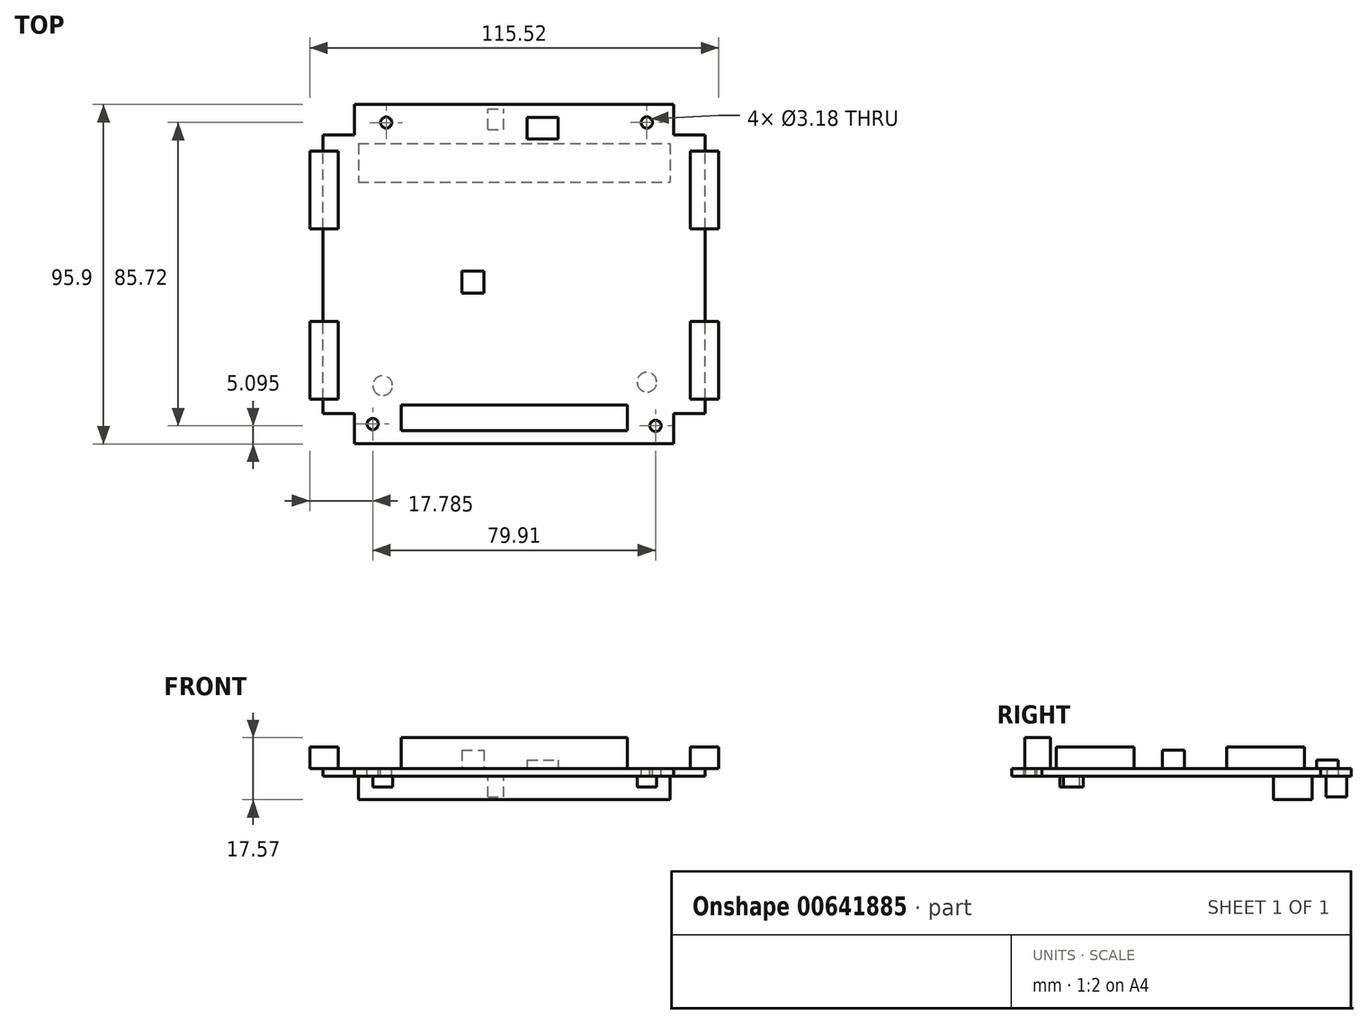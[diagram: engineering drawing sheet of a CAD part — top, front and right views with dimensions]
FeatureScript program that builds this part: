
annotation { "Feature Type Name" : "Feature", "Feature Type Description" : "" }
export const myFeature = defineFeature(function(context is Context, id is Id, definition is map)
    precondition{}
    {
        {
            var Q0;
            Q0=qCreatedBy(makeId("Top.planeOp"),FACE);
            var sketch = newSketch(context, id + "F0", { "sketchPlane" : qUnion([Q0])});
            skLineSegment(sketch, "E0.bottom", {"start": v(53.98, -39.42) * mm, "end": v(-53.97, -39.42) * mm});
            skLineSegment(sketch, "E0.top", {"start": v(53.97, 39.42) * mm, "end": v(-53.98, 39.42) * mm});
            skLineSegment(sketch, "E0.left", {"start": v(53.98, -39.42) * mm, "end": v(53.97, 39.42) * mm});
            skLineSegment(sketch, "E0.right", {"start": v(-53.97, -39.42) * mm, "end": v(-53.98, 39.42) * mm});
            skPoint(sketch, "E0.middle", {"position": v(0, 0) * mm});
            skLineSegment(sketch, "E1.bottom", {"start": v(45.09, -47.95) * mm, "end": v(-45.09, -47.95) * mm});
            skLineSegment(sketch, "E1.top", {"start": v(45.09, 47.95) * mm, "end": v(-45.09, 47.94) * mm});
            skLineSegment(sketch, "E1.left", {"start": v(45.09, -47.95) * mm, "end": v(45.09, 47.95) * mm});
            skLineSegment(sketch, "E1.right", {"start": v(-45.09, -47.95) * mm, "end": v(-45.09, 47.94) * mm});
            skSolve(sketch);
        }
        {
            var Q0;
            Q0 = qSketchRegion(id + "F0", true);
            extrude(context, id + "F1", {"entities" : qUnion([Q0]), "depth" : 2.24 * mm, "offsetDistance" : 25 * mm});
        }
        {
            var Q0;
            Q0=makeQuery(id+"F1.opExtrude","CAP_FACE",FACE,{"disambiguationData":[OSD([sQuery(id+"F0.wireOp",EDGE,"E0.bottom"),sQuery(id+"F0.wireOp",EDGE,"E0.top"),sQuery(id+"F0.wireOp",EDGE,"E0.left"),sQuery(id+"F0.wireOp",EDGE,"E0.right"),sQuery(id+"F0.wireOp",EDGE,"E1.bottom"),sQuery(id+"F0.wireOp",EDGE,"E1.top"),sQuery(id+"F0.wireOp",EDGE,"E1.left"),sQuery(id+"F0.wireOp",EDGE,"E1.right")])],"isStart":false});
            var sketch = newSketch(context, id + "F2", { "sketchPlane" : qUnion([Q0])});
            skLineSegment(sketch, "E2.bottom", {"start": v(49.72, -35.28) * mm, "end": v(57.76, -35.28) * mm});
            skLineSegment(sketch, "E2.top", {"start": v(49.72, -13.28) * mm, "end": v(57.76, -13.28) * mm});
            skLineSegment(sketch, "E2.left", {"start": v(49.72, -35.28) * mm, "end": v(49.72, -13.28) * mm});
            skLineSegment(sketch, "E2.right", {"start": v(57.76, -35.28) * mm, "end": v(57.76, -13.28) * mm});
            skSolve(sketch);
        }
        {
            var Q0;
            Q0 = qSketchRegion(id + "F2", true);
            extrude(context, id + "F3", {"entities" : qUnion([Q0]), "depth" : 6.05 * mm, "offsetDistance" : 25 * mm});
        }
        {
            var Q0;
            Q0=makeQuery(id+"F1.opExtrude","CAP_FACE",FACE,{"disambiguationData":[OSD([sQuery(id+"F0.wireOp",EDGE,"E0.bottom"),sQuery(id+"F0.wireOp",EDGE,"E0.top"),sQuery(id+"F0.wireOp",EDGE,"E0.left"),sQuery(id+"F0.wireOp",EDGE,"E0.right"),sQuery(id+"F0.wireOp",EDGE,"E1.bottom"),sQuery(id+"F0.wireOp",EDGE,"E1.top"),sQuery(id+"F0.wireOp",EDGE,"E1.left"),sQuery(id+"F0.wireOp",EDGE,"E1.right")])],"isStart":false});
            var sketch = newSketch(context, id + "F4", { "sketchPlane" : qUnion([Q0])});
            skLineSegment(sketch, "E3.bottom", {"start": v(49.72, 34.82) * mm, "end": v(57.76, 34.82) * mm});
            skLineSegment(sketch, "E3.top", {"start": v(49.72, 12.82) * mm, "end": v(57.76, 12.82) * mm});
            skLineSegment(sketch, "E3.left", {"start": v(49.72, 34.82) * mm, "end": v(49.72, 12.82) * mm});
            skLineSegment(sketch, "E3.right", {"start": v(57.76, 34.82) * mm, "end": v(57.76, 12.82) * mm});
            skSolve(sketch);
        }
        {
            var Q0;
            Q0 = qSketchRegion(id + "F4", true);
            extrude(context, id + "F5", {"entities" : qUnion([Q0]), "depth" : 6.05 * mm, "offsetDistance" : 25 * mm});
        }
        {
            var Q0;
            Q0=makeQuery(id+"F5.opExtrude","SWEPT_BODY",BODY,{"disambiguationData":[OSD([sQuery(id+"F4.wireOp",EDGE,"E3.bottom"),sQuery(id+"F4.wireOp",EDGE,"E3.top"),sQuery(id+"F4.wireOp",EDGE,"E3.left"),sQuery(id+"F4.wireOp",EDGE,"E3.right")])]});
            var Q1;
            Q1=makeQuery(id+"F3.opExtrude","SWEPT_BODY",BODY,{"disambiguationData":[OSD([sQuery(id+"F2.wireOp",EDGE,"E2.bottom"),sQuery(id+"F2.wireOp",EDGE,"E2.top"),sQuery(id+"F2.wireOp",EDGE,"E2.left"),sQuery(id+"F2.wireOp",EDGE,"E2.right")])]});
            var Q2;
            Q2=qCreatedBy(makeId("Right.planeOp"),FACE);
            mirror(context, id + "F6", {"operationType" : NewBodyOperationType.ADD, "entities" : qUnion([Q0, Q1]), "mirrorPlane" : qUnion([Q2])});
        }
        {
            var Q0;
            Q0=makeQuery(id+"F1.opExtrude","CAP_FACE",FACE,{"disambiguationData":[OSD([sQuery(id+"F0.wireOp",EDGE,"E0.bottom"),sQuery(id+"F0.wireOp",EDGE,"E0.top"),sQuery(id+"F0.wireOp",EDGE,"E0.left"),sQuery(id+"F0.wireOp",EDGE,"E0.right"),sQuery(id+"F0.wireOp",EDGE,"E1.bottom"),sQuery(id+"F0.wireOp",EDGE,"E1.top"),sQuery(id+"F0.wireOp",EDGE,"E1.left"),sQuery(id+"F0.wireOp",EDGE,"E1.right")])],"isStart":false});
            var sketch = newSketch(context, id + "F7", { "sketchPlane" : qUnion([Q0])});
            skLineSegment(sketch, "E4.bottom", {"start": v(-31.88, -36.96) * mm, "end": v(32, -36.96) * mm});
            skLineSegment(sketch, "E4.top", {"start": v(-31.88, -44.22) * mm, "end": v(32, -44.22) * mm});
            skLineSegment(sketch, "E4.left", {"start": v(-31.88, -36.96) * mm, "end": v(-31.88, -44.22) * mm});
            skLineSegment(sketch, "E4.right", {"start": v(32, -36.96) * mm, "end": v(32, -44.22) * mm});
            skSolve(sketch);
        }
        {
            var Q0;
            Q0 = qSketchRegion(id + "F7", true);
            extrude(context, id + "F8", {"entities" : qUnion([Q0]), "operationType" : NewBodyOperationType.ADD, "depth" : 8.7 * mm, "offsetDistance" : 25 * mm});
        }
        {
            var Q0;
            Q0=makeQuery(id+"F1.opExtrude","CAP_FACE",FACE,{"disambiguationData":[OSD([sQuery(id+"F0.wireOp",EDGE,"E0.bottom"),sQuery(id+"F0.wireOp",EDGE,"E0.top"),sQuery(id+"F0.wireOp",EDGE,"E0.left"),sQuery(id+"F0.wireOp",EDGE,"E0.right"),sQuery(id+"F0.wireOp",EDGE,"E1.bottom"),sQuery(id+"F0.wireOp",EDGE,"E1.top"),sQuery(id+"F0.wireOp",EDGE,"E1.left"),sQuery(id+"F0.wireOp",EDGE,"E1.right")])],"isStart":false});
            var sketch = newSketch(context, id + "F9", { "sketchPlane" : qUnion([Q0])});
            skLineSegment(sketch, "E5.bottom", {"start": v(-14.78, 0.87) * mm, "end": v(-8.53, 0.87) * mm});
            skLineSegment(sketch, "E5.top", {"start": v(-14.78, -5.38) * mm, "end": v(-8.53, -5.38) * mm});
            skLineSegment(sketch, "E5.left", {"start": v(-14.78, 0.87) * mm, "end": v(-14.78, -5.38) * mm});
            skLineSegment(sketch, "E5.right", {"start": v(-8.53, 0.87) * mm, "end": v(-8.53, -5.38) * mm});
            skSolve(sketch);
        }
        {
            var Q0;
            Q0 = qSketchRegion(id + "F9", true);
            extrude(context, id + "F10", {"entities" : qUnion([Q0]), "operationType" : NewBodyOperationType.ADD, "depth" : 5.15 * mm, "offsetDistance" : 25 * mm});
        }
        {
            var Q0;
            Q0=makeQuery(id+"F1.opExtrude","CAP_FACE",FACE,{"disambiguationData":[OSD([sQuery(id+"F0.wireOp",EDGE,"E0.bottom"),sQuery(id+"F0.wireOp",EDGE,"E0.top"),sQuery(id+"F0.wireOp",EDGE,"E0.left"),sQuery(id+"F0.wireOp",EDGE,"E0.right"),sQuery(id+"F0.wireOp",EDGE,"E1.bottom"),sQuery(id+"F0.wireOp",EDGE,"E1.top"),sQuery(id+"F0.wireOp",EDGE,"E1.left"),sQuery(id+"F0.wireOp",EDGE,"E1.right")])],"isStart":false});
            var sketch = newSketch(context, id + "F11", { "sketchPlane" : qUnion([Q0])});
            skLineSegment(sketch, "E6.bottom", {"start": v(3.63, 44.31) * mm, "end": v(12.37, 44.31) * mm});
            skLineSegment(sketch, "E6.top", {"start": v(3.63, 38.2) * mm, "end": v(12.38, 38.2) * mm});
            skLineSegment(sketch, "E6.left", {"start": v(3.63, 44.31) * mm, "end": v(3.63, 38.2) * mm});
            skLineSegment(sketch, "E6.right", {"start": v(12.37, 44.31) * mm, "end": v(12.38, 38.2) * mm});
            skSolve(sketch);
        }
        {
            var Q0;
            Q0 = qSketchRegion(id + "F11", true);
            extrude(context, id + "F12", {"entities" : qUnion([Q0]), "operationType" : NewBodyOperationType.ADD, "depth" : 2.4 * mm, "offsetDistance" : 25 * mm});
        }
        {
            var Q0;
            Q0=makeQuery(id+"F1.opExtrude","CAP_FACE",FACE,{"disambiguationData":[OSD([sQuery(id+"F0.wireOp",EDGE,"E0.bottom"),sQuery(id+"F0.wireOp",EDGE,"E0.top"),sQuery(id+"F0.wireOp",EDGE,"E0.left"),sQuery(id+"F0.wireOp",EDGE,"E0.right"),sQuery(id+"F0.wireOp",EDGE,"E1.bottom"),sQuery(id+"F0.wireOp",EDGE,"E1.top"),sQuery(id+"F0.wireOp",EDGE,"E1.left"),sQuery(id+"F0.wireOp",EDGE,"E1.right")])],"isStart":true});
            var sketch = newSketch(context, id + "F13", { "sketchPlane" : qUnion([Q0])});
            skLineSegment(sketch, "E7.bottom", {"start": v(-44, -36.95) * mm, "end": v(44, -36.95) * mm});
            skLineSegment(sketch, "E7.top", {"start": v(-44, -26) * mm, "end": v(44, -26) * mm});
            skLineSegment(sketch, "E7.left", {"start": v(-44, -36.95) * mm, "end": v(-44, -26) * mm});
            skLineSegment(sketch, "E7.right", {"start": v(44, -36.95) * mm, "end": v(44, -26) * mm});
            skSolve(sketch);
        }
        {
            var Q0;
            Q0 = qSketchRegion(id + "F13", true);
            extrude(context, id + "F14", {"entities" : qUnion([Q0]), "operationType" : NewBodyOperationType.ADD, "depth" : 6.63 * mm, "offsetDistance" : 25 * mm});
        }
        {
            var Q0;
            Q0 = qSketchRegion(id + "F11", true);
            extrude(context, id + "F15", {"entities" : qUnion([Q0]), "depth" : 2.4 * mm, "offsetDistance" : 25 * mm});
        }
        {
            var Q0;
            Q0=makeQuery(id+"F1.opExtrude","CAP_FACE",FACE,{"disambiguationData":[OSD([sQuery(id+"F0.wireOp",EDGE,"E0.bottom"),sQuery(id+"F0.wireOp",EDGE,"E0.top"),sQuery(id+"F0.wireOp",EDGE,"E0.left"),sQuery(id+"F0.wireOp",EDGE,"E0.right"),sQuery(id+"F0.wireOp",EDGE,"E1.bottom"),sQuery(id+"F0.wireOp",EDGE,"E1.top"),sQuery(id+"F0.wireOp",EDGE,"E1.left"),sQuery(id+"F0.wireOp",EDGE,"E1.right")])],"isStart":true});
            var sketch = newSketch(context, id + "F16", { "sketchPlane" : qUnion([Q0])});
            skLineSegment(sketch, "E8.bottom", {"start": v(-7.44, -40.88) * mm, "end": v(-3, -40.88) * mm});
            skLineSegment(sketch, "E8.top", {"start": v(-7.44, -46.68) * mm, "end": v(-3, -46.68) * mm});
            skLineSegment(sketch, "E8.left", {"start": v(-7.44, -40.88) * mm, "end": v(-7.44, -46.68) * mm});
            skLineSegment(sketch, "E8.right", {"start": v(-3, -40.88) * mm, "end": v(-3, -46.68) * mm});
            skSolve(sketch);
        }
        {
            var Q0;
            Q0 = qSketchRegion(id + "F16", true);
            extrude(context, id + "F17", {"entities" : qUnion([Q0]), "operationType" : NewBodyOperationType.ADD, "depth" : 5.86 * mm, "offsetDistance" : 25 * mm});
        }
        {
            var Q0;
            Q0=makeQuery(id+"F1.opExtrude","CAP_FACE",FACE,{"disambiguationData":[OSD([sQuery(id+"F0.wireOp",EDGE,"E0.bottom"),sQuery(id+"F0.wireOp",EDGE,"E0.top"),sQuery(id+"F0.wireOp",EDGE,"E0.left"),sQuery(id+"F0.wireOp",EDGE,"E0.right"),sQuery(id+"F0.wireOp",EDGE,"E1.bottom"),sQuery(id+"F0.wireOp",EDGE,"E1.top"),sQuery(id+"F0.wireOp",EDGE,"E1.left"),sQuery(id+"F0.wireOp",EDGE,"E1.right")])],"isStart":true});
            var sketch = newSketch(context, id + "F18", { "sketchPlane" : qUnion([Q0])});
            skCircle(sketch, "E9", {"center": v(-37.16, 31.5) * mm, "radius": 2.78 * mm});
            skSolve(sketch);
        }
        {
            var Q0;
            Q0 = qSketchRegion(id + "F18", true);
            extrude(context, id + "F19", {"entities" : qUnion([Q0]), "operationType" : NewBodyOperationType.ADD, "depth" : 2.98 * mm, "offsetDistance" : 25 * mm});
        }
        {
            var Q0;
            Q0=makeQuery(id+"F1.opExtrude","CAP_FACE",FACE,{"disambiguationData":[OSD([sQuery(id+"F0.wireOp",EDGE,"E0.bottom"),sQuery(id+"F0.wireOp",EDGE,"E0.top"),sQuery(id+"F0.wireOp",EDGE,"E0.left"),sQuery(id+"F0.wireOp",EDGE,"E0.right"),sQuery(id+"F0.wireOp",EDGE,"E1.bottom"),sQuery(id+"F0.wireOp",EDGE,"E1.top"),sQuery(id+"F0.wireOp",EDGE,"E1.left"),sQuery(id+"F0.wireOp",EDGE,"E1.right")])],"isStart":true});
            var sketch = newSketch(context, id + "F20", { "sketchPlane" : qUnion([Q0])});
            skCircle(sketch, "E10", {"center": v(37.5, 30.5) * mm, "radius": 2.78 * mm});
            skSolve(sketch);
        }
        {
            var Q0;
            Q0 = qSketchRegion(id + "F20", true);
            extrude(context, id + "F21", {"entities" : qUnion([Q0]), "operationType" : NewBodyOperationType.ADD, "depth" : 2.98 * mm, "offsetDistance" : 25 * mm});
        }
        {
            var Q0;
            Q0=makeQuery(id+"F1.opExtrude","CAP_FACE",FACE,{"disambiguationData":[OSD([sQuery(id+"F0.wireOp",EDGE,"E0.bottom"),sQuery(id+"F0.wireOp",EDGE,"E0.top"),sQuery(id+"F0.wireOp",EDGE,"E0.left"),sQuery(id+"F0.wireOp",EDGE,"E0.right"),sQuery(id+"F0.wireOp",EDGE,"E1.bottom"),sQuery(id+"F0.wireOp",EDGE,"E1.top"),sQuery(id+"F0.wireOp",EDGE,"E1.left"),sQuery(id+"F0.wireOp",EDGE,"E1.right")])],"isStart":false});
            var sketch = newSketch(context, id + "F22", { "sketchPlane" : qUnion([Q0])});
            skCircle(sketch, "E11", {"center": v(39.93, -42.86) * mm, "radius": 1.59 * mm});
            skCircle(sketch, "E12", {"center": v(-39.97, -42.35) * mm, "radius": 1.59 * mm});
            skCircle(sketch, "E13", {"center": v(-36.17, 42.85) * mm, "radius": 1.59 * mm});
            skCircle(sketch, "E14", {"center": v(37.46, 42.87) * mm, "radius": 1.59 * mm});
            skSolve(sketch);
        }
        {
            var Q0;
            Q0 = qSketchRegion(id + "F22", true);
            extrude(context, id + "F23", {"entities" : qUnion([Q0]), "operationType" : NewBodyOperationType.REMOVE, "oppositeDirection" : true, "depth" : 25 * mm, "offsetDistance" : 25 * mm});
        }
    });
